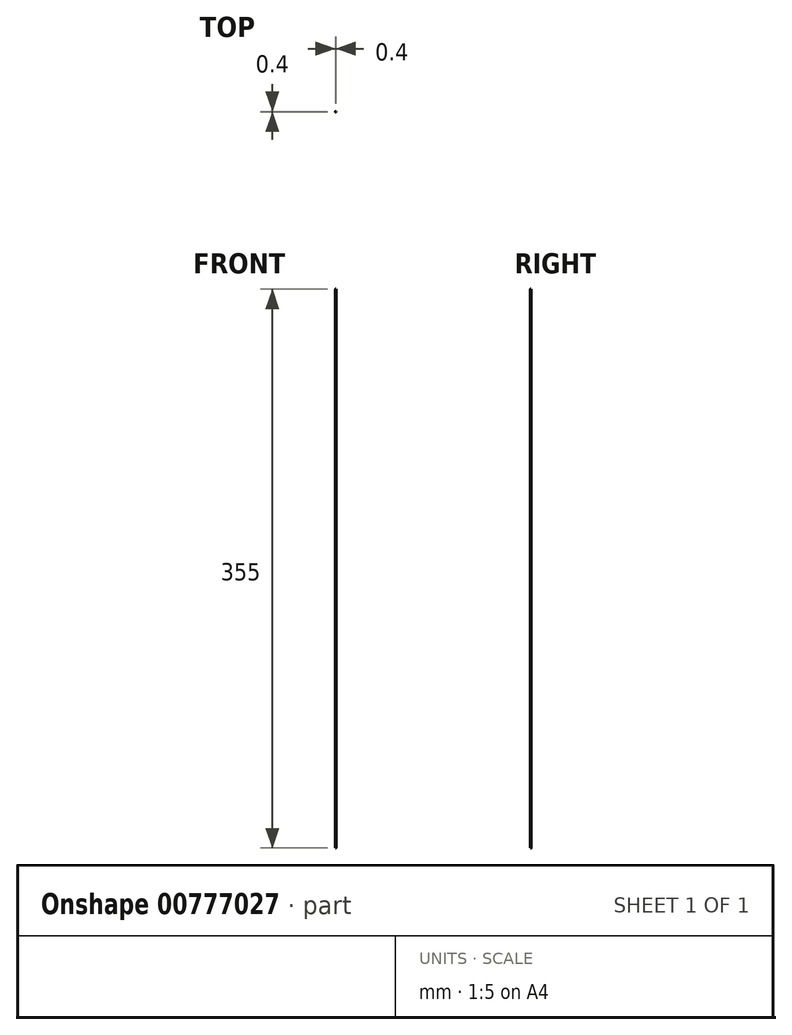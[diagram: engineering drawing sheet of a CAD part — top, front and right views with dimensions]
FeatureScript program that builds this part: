
annotation { "Feature Type Name" : "Feature", "Feature Type Description" : "" }
export const myFeature = defineFeature(function(context is Context, id is Id, definition is map)
    precondition{}
    {
        {
            var Q0;
            Q0=qCreatedBy(makeId("Top.planeOp"),FACE);
            var sketch = newSketch(context, id + "F0", { "sketchPlane" : qUnion([Q0])});
            skCircle(sketch, "E0", {"center": v(0, 0) * mm, "radius": 0.2 * mm});
            skSolve(sketch);
        }
        {
            var Q0;
            Q0=qSketchRegion(id+"F0",true);
            extrude(context, id + "F1", {"entities" : qUnion([Q0]), "depth" : 355 * mm, "offsetDistance" : 25 * mm});
        }
    });
